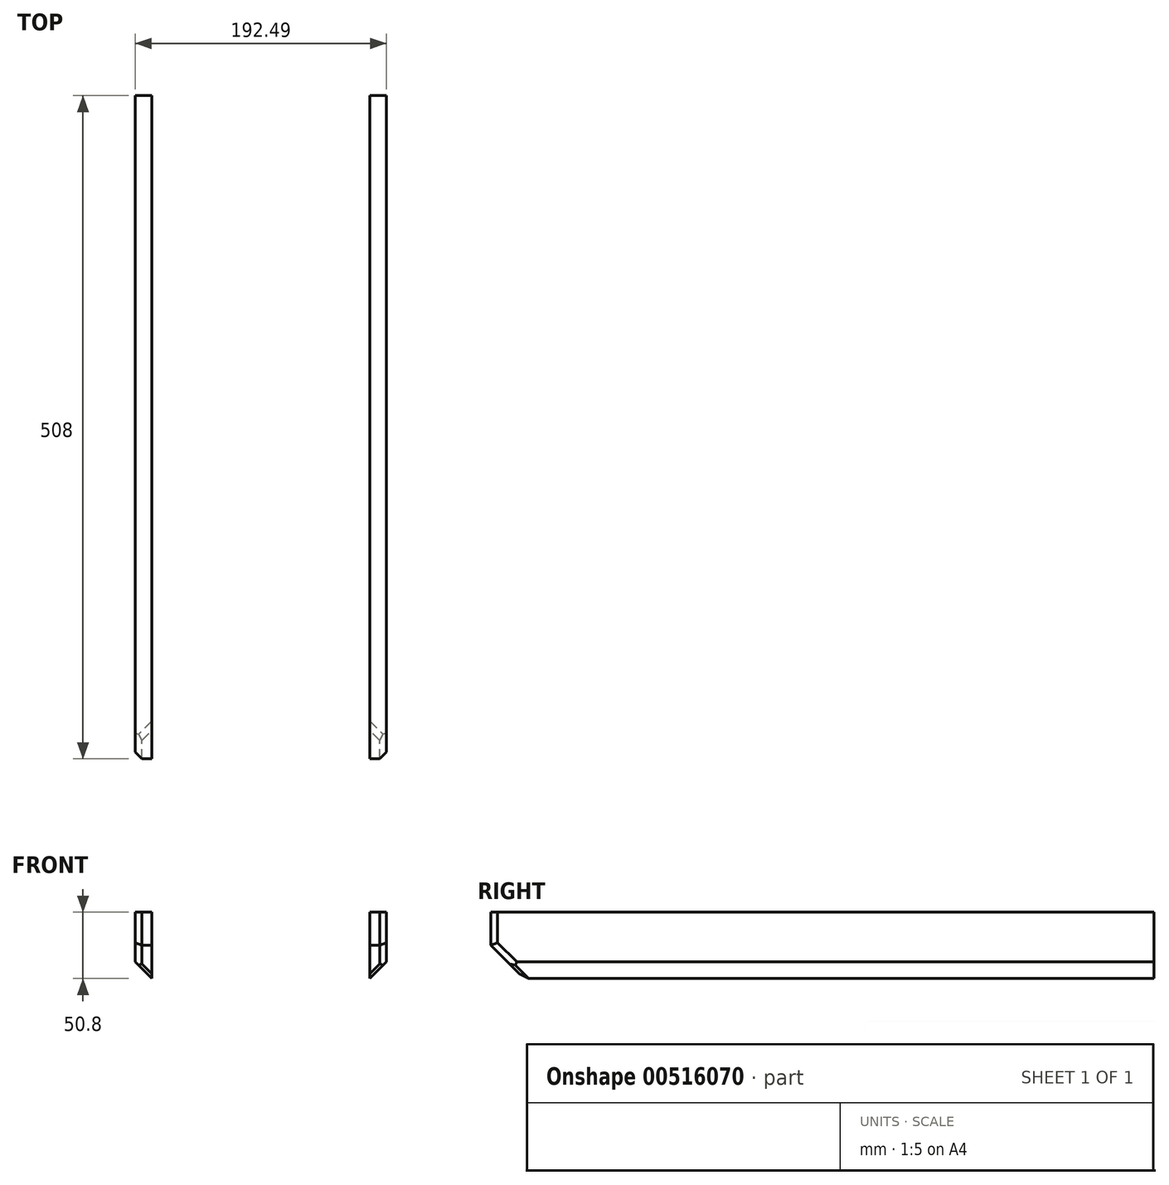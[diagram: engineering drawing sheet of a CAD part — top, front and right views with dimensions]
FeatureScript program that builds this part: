
annotation { "Feature Type Name" : "Feature", "Feature Type Description" : "" }
export const myFeature = defineFeature(function(context is Context, id is Id, definition is map)
    precondition{}
    {
        {
            var Q0;
            Q0=qCreatedBy(makeId("Top.planeOp"),FACE);
            var sketch = newSketch(context, id + "F0", { "sketchPlane" : qUnion([Q0])});
            skLineSegment(sketch, "E0.bottom", {"start": v(6.35, -254) * mm, "end": v(-6.35, -254) * mm});
            skLineSegment(sketch, "E0.top", {"start": v(6.35, 254) * mm, "end": v(-6.35, 254) * mm});
            skLineSegment(sketch, "E0.left", {"start": v(6.35, -254) * mm, "end": v(6.35, 254) * mm});
            skLineSegment(sketch, "E0.right", {"start": v(-6.35, -254) * mm, "end": v(-6.35, 254) * mm});
            skPoint(sketch, "E0.middle", {"position": v(0, 0) * mm});
            skLineSegment(sketch, "E1", {"start": v(89.9, -344.94) * mm, "end": v(89.9, 298.27) * mm, "construction": true});
            skPoint(sketch, "E2.MirrorP", {"position": v(179.79, 0) * mm});
            skLineSegment(sketch, "E3.MirrorCS", {"start": v(173.44, -254) * mm, "end": v(186.14, -254) * mm});
            skLineSegment(sketch, "E4.MirrorCS", {"start": v(173.44, 254) * mm, "end": v(186.14, 254) * mm});
            skLineSegment(sketch, "E5.MirrorCS", {"start": v(173.44, -254) * mm, "end": v(173.44, 254) * mm});
            skLineSegment(sketch, "E6.MirrorCS", {"start": v(186.14, -254) * mm, "end": v(186.14, 254) * mm});
            skSolve(sketch);
        }
        {
            var Q0;
            Q0=makeQuery(id+"F0.imprint","IMPRINT",FACE,{"disambiguationData":[TD([[makeQuery(id+"F0.imprint","IMPRINT",EDGE,{"derivedFrom":sQuery(id+"F0.wireOp",EDGE,"E0.bottom")}),-1.0]])]});
            extrude(context, id + "F1", {"entities" : qUnion([Q0]), "depth" : 50.8 * mm, "offsetDistance" : 25.4 * mm});
        }
        {
            var Q0;
            Q0=makeQuery(id+"F1.opExtrude","CAP_EDGE",EDGE,{"disambiguationData":[OSD([sQuery(id+"F0.wireOp",EDGE,"E0.bottom")])],"isStart":true});
            chamfer(context, id + "F2", {"entities" : qUnion([Q0]), "width" : 25.4 * mm, "tangentPropagation" : true});
        }
        {
            var Q0;
            Q0=makeQuery(id+"F1.opExtrude","CAP_EDGE",EDGE,{"disambiguationData":[OSD([sQuery(id+"F0.wireOp",EDGE,"E0.right")])],"isStart":true});
            chamfer(context, id + "F3", {"entities" : qUnion([Q0]), "width" : 12.7 * mm, "tangentPropagation" : true});
        }
        {
            var Q0;
            Q0=makeQuery(id+"F0.imprint","IMPRINT",FACE,{"disambiguationData":[TD([[makeQuery(id+"F0.imprint","IMPRINT",EDGE,{"derivedFrom":sQuery(id+"F0.wireOp",EDGE,"E3.MirrorCS")}),1.0]])]});
            extrude(context, id + "F4", {"entities" : qUnion([Q0]), "depth" : 50.8 * mm, "offsetDistance" : 25.4 * mm});
        }
        {
            var Q0;
            Q0=makeQuery(id+"F4.opExtrude","CAP_EDGE",EDGE,{"disambiguationData":[OSD([sQuery(id+"F0.wireOp",EDGE,"E3.MirrorCS")])],"isStart":true});
            chamfer(context, id + "F5", {"entities" : qUnion([Q0]), "width" : 25.4 * mm, "tangentPropagation" : true});
        }
        {
            var Q0;
            Q0=makeQuery(id+"F4.opExtrude","CAP_EDGE",EDGE,{"disambiguationData":[OSD([sQuery(id+"F0.wireOp",EDGE,"E6.MirrorCS")])],"isStart":true});
            chamfer(context, id + "F6", {"entities" : qUnion([Q0]), "width" : 12.7 * mm, "tangentPropagation" : true});
        }
        {
            var Q0;
            Q0=makeQuery(id+"F1.opExtrude","SWEPT_EDGE",EDGE,{"disambiguationData":[OSD([sQuery(id+"F0.wireOp",EDGE,"E0.bottom"),sQuery(id+"F0.wireOp",EDGE,"E0.right")])]});
            var Q1;
            Q1=makeQuery(id+"F2.opChamfer","BLEND_EDGE",EDGE,{"blendedFrom":[makeQuery(id+"F1.opExtrude","CAP_EDGE",EDGE,{"disambiguationData":[OSD([sQuery(id+"F0.wireOp",EDGE,"E0.bottom")])],"isStart":true}),makeQuery(id+"F1.opExtrude","SWEPT_FACE",FACE,{"disambiguationData":[OSD([sQuery(id+"F0.wireOp",EDGE,"E0.right")])]})],"blendedInto":[makeQuery(id+"F1.opExtrude","SWEPT_FACE",FACE,{"disambiguationData":[OSD([sQuery(id+"F0.wireOp",EDGE,"E0.right")])]})]});
            var Q2;
            Q2=makeQuery(id+"F3.opChamfer","BLEND_EDGE",EDGE,{"blendedFrom":[makeQuery(id+"F1.opExtrude","CAP_EDGE",EDGE,{"disambiguationData":[OSD([sQuery(id+"F0.wireOp",EDGE,"E0.right")])],"isStart":true}),makeQuery(id+"F2.opChamfer","BLEND_FACE",FACE,{"disambiguationData":[OSD([sQuery(id+"F0.wireOp",EDGE,"E0.bottom")])]})],"blendedInto":[makeQuery(id+"F2.opChamfer","BLEND_FACE",FACE,{"disambiguationData":[OSD([sQuery(id+"F0.wireOp",EDGE,"E0.bottom")])]})]});
            var Q3;
            {var subQ0=sQuery(id+"F0.wireOp",EDGE,"E0.bottom");Q3=makeQuery(id+"F2.opChamfer","BLEND_EDGE",EDGE,{"blendedFrom":[makeQuery(id+"F1.opExtrude","CAP_EDGE",EDGE,{"disambiguationData":[OSD([subQ0])],"isStart":true}),makeQuery(id+"F1.opExtrude","CAP_FACE",FACE,{"disambiguationData":[OSD([subQ0,sQuery(id+"F0.wireOp",EDGE,"E0.top"),sQuery(id+"F0.wireOp",EDGE,"E0.left"),sQuery(id+"F0.wireOp",EDGE,"E0.right")])],"isStart":true})],"blendedInto":[makeQuery(id+"F1.opExtrude","CAP_FACE",FACE,{"disambiguationData":[OSD([subQ0,sQuery(id+"F0.wireOp",EDGE,"E0.top"),sQuery(id+"F0.wireOp",EDGE,"E0.left"),sQuery(id+"F0.wireOp",EDGE,"E0.right")])],"isStart":true})]});}
            var Q4;
            Q4=makeQuery(id+"F4.opExtrude","SWEPT_EDGE",EDGE,{"disambiguationData":[OSD([sQuery(id+"F0.wireOp",EDGE,"E3.MirrorCS"),sQuery(id+"F0.wireOp",EDGE,"E6.MirrorCS")])]});
            var Q5;
            Q5=makeQuery(id+"F5.opChamfer","BLEND_EDGE",EDGE,{"blendedFrom":[makeQuery(id+"F4.opExtrude","CAP_EDGE",EDGE,{"disambiguationData":[OSD([sQuery(id+"F0.wireOp",EDGE,"E3.MirrorCS")])],"isStart":true}),makeQuery(id+"F4.opExtrude","SWEPT_FACE",FACE,{"disambiguationData":[OSD([sQuery(id+"F0.wireOp",EDGE,"E6.MirrorCS")])]})],"blendedInto":[makeQuery(id+"F4.opExtrude","SWEPT_FACE",FACE,{"disambiguationData":[OSD([sQuery(id+"F0.wireOp",EDGE,"E6.MirrorCS")])]})]});
            var Q6;
            Q6=makeQuery(id+"F6.opChamfer","BLEND_EDGE",EDGE,{"blendedFrom":[makeQuery(id+"F4.opExtrude","CAP_EDGE",EDGE,{"disambiguationData":[OSD([sQuery(id+"F0.wireOp",EDGE,"E6.MirrorCS")])],"isStart":true}),makeQuery(id+"F5.opChamfer","BLEND_FACE",FACE,{"disambiguationData":[OSD([sQuery(id+"F0.wireOp",EDGE,"E3.MirrorCS")])]})],"blendedInto":[makeQuery(id+"F5.opChamfer","BLEND_FACE",FACE,{"disambiguationData":[OSD([sQuery(id+"F0.wireOp",EDGE,"E3.MirrorCS")])]})]});
            var Q7;
            {var subQ0=sQuery(id+"F0.wireOp",EDGE,"E3.MirrorCS");Q7=makeQuery(id+"F5.opChamfer","BLEND_EDGE",EDGE,{"blendedFrom":[makeQuery(id+"F4.opExtrude","CAP_EDGE",EDGE,{"disambiguationData":[OSD([subQ0])],"isStart":true}),makeQuery(id+"F4.opExtrude","CAP_FACE",FACE,{"disambiguationData":[OSD([subQ0,sQuery(id+"F0.wireOp",EDGE,"E4.MirrorCS"),sQuery(id+"F0.wireOp",EDGE,"E5.MirrorCS"),sQuery(id+"F0.wireOp",EDGE,"E6.MirrorCS")])],"isStart":true})],"blendedInto":[makeQuery(id+"F4.opExtrude","CAP_FACE",FACE,{"disambiguationData":[OSD([subQ0,sQuery(id+"F0.wireOp",EDGE,"E4.MirrorCS"),sQuery(id+"F0.wireOp",EDGE,"E5.MirrorCS"),sQuery(id+"F0.wireOp",EDGE,"E6.MirrorCS")])],"isStart":true})]});}
            chamfer(context, id + "F7", {"entities" : qUnion([Q0, Q1, Q2, Q3, Q4, Q5, Q6, Q7]), "width" : 5.08 * mm, "tangentPropagation" : true});
        }
    });
